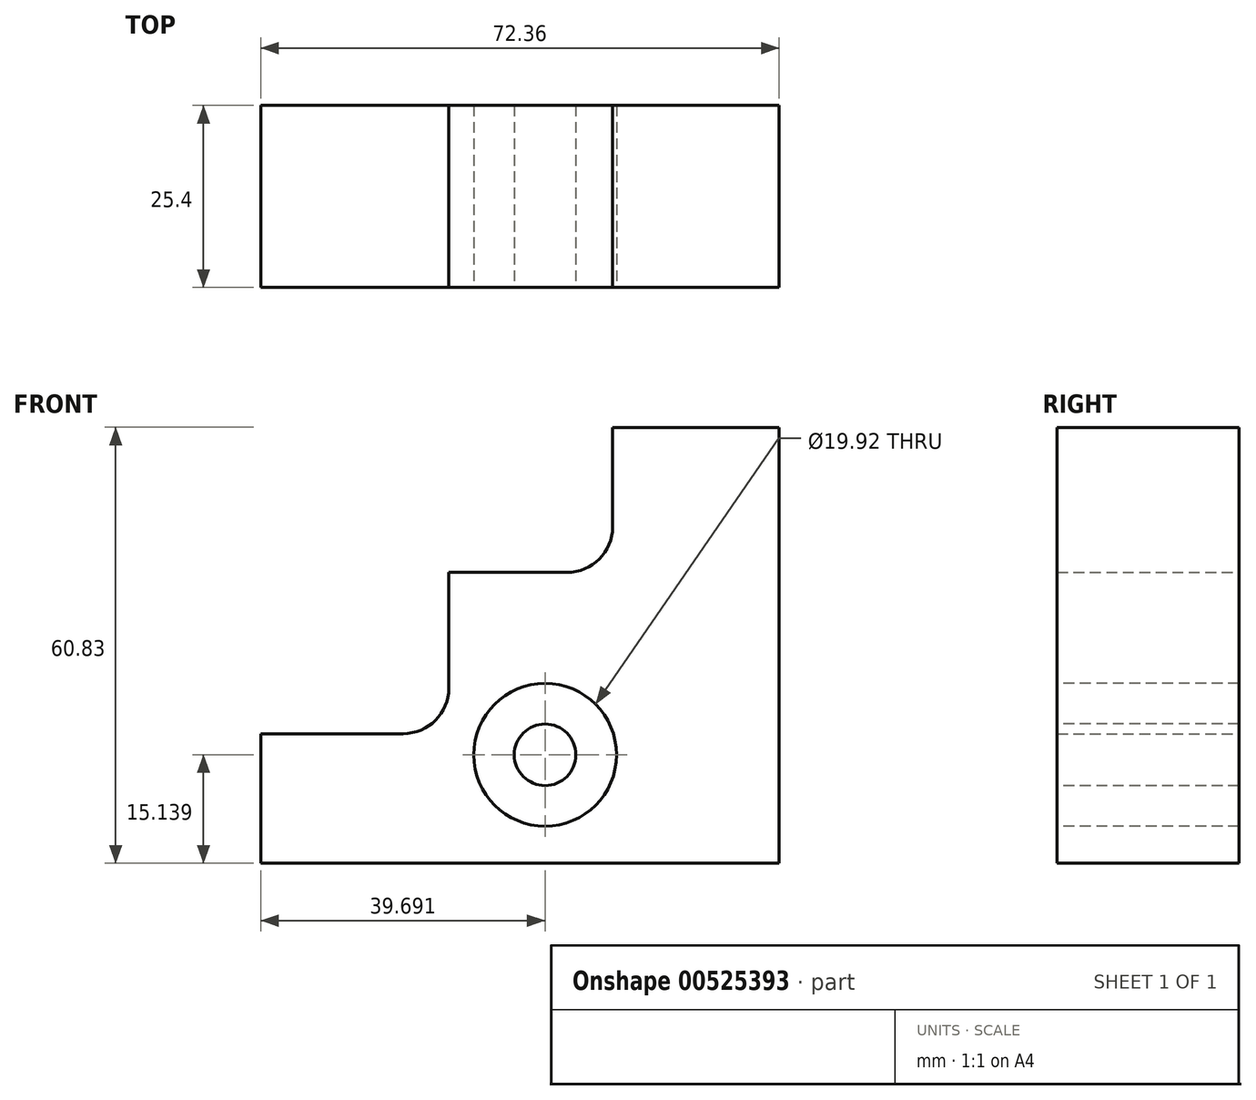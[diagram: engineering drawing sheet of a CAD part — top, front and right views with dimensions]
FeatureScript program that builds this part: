
annotation { "Feature Type Name" : "Feature", "Feature Type Description" : "" }
export const myFeature = defineFeature(function(context is Context, id is Id, definition is map)
    precondition{}
    {
        {
            var Q0;
            Q0=qCreatedBy(makeId("Front.planeOp"),FACE);
            var sketch = newSketch(context, id + "F0", { "sketchPlane" : qUnion([Q0])});
            skLineSegment(sketch, "E0", {"start": v(-54.48, 0) * mm, "end": v(-54.48, 18.09) * mm});
            skLineSegment(sketch, "E1", {"start": v(-54.48, 18.09) * mm, "end": v(-34.58, 18.09) * mm});
            skLineSegment(sketch, "E2", {"start": v(-28.23, 24.44) * mm, "end": v(-28.23, 40.58) * mm});
            skLineSegment(sketch, "E3", {"start": v(-27.48, 40.58) * mm, "end": v(-11.71, 40.58) * mm});
            skLineSegment(sketch, "E4", {"start": v(-5.36, 46.93) * mm, "end": v(-5.36, 60.83) * mm});
            skLineSegment(sketch, "E5", {"start": v(-5.36, 60.83) * mm, "end": v(17.88, 60.83) * mm});
            skLineSegment(sketch, "E6", {"start": v(17.88, 60.83) * mm, "end": v(17.88, 58.95) * mm});
            skLineSegment(sketch, "E7", {"start": v(17.88, 58.95) * mm, "end": v(17.88, 0) * mm});
            skLineSegment(sketch, "E8", {"start": v(17.88, 0) * mm, "end": v(-54.48, 0) * mm});
            skPoint(sketch, "E9.visualSharp", {"position": v(-28.23, 18.09) * mm});
            skArc(sketch, "E9.filletArc", {"start": v(-34.58, 18.09) * mm, "mid": v(-30.1, 19.95) * mm, "end": v(-28.23, 24.44) * mm});
            skPoint(sketch, "E10.visualSharp", {"position": v(-5.36, 40.58) * mm});
            skArc(sketch, "E10.filletArc", {"start": v(-11.71, 40.58) * mm, "mid": v(-7.22, 42.44) * mm, "end": v(-5.36, 46.93) * mm});
            skLineSegment(sketch, "E11", {"start": v(-28.23, 40.58) * mm, "end": v(-27.48, 40.58) * mm});
            skSolve(sketch);
        }
        {
            var Q0;
            Q0 = qSketchRegion(id + "F0", true);
            extrude(context, id + "F1", {"entities" : qUnion([Q0]), "depth" : 25.4 * mm, "offsetDistance" : 25.4 * mm});
        }
        {
            var Q0;
            Q0=makeQuery(id+"F1.opExtrude","CAP_FACE",FACE,{"disambiguationData":[OSD([sQuery(id+"F0.wireOp",EDGE,"E0"),sQuery(id+"F0.wireOp",EDGE,"E1"),sQuery(id+"F0.wireOp",EDGE,"E2"),sQuery(id+"F0.wireOp",EDGE,"E3"),sQuery(id+"F0.wireOp",EDGE,"E4"),sQuery(id+"F0.wireOp",EDGE,"E5"),sQuery(id+"F0.wireOp",EDGE,"E6"),sQuery(id+"F0.wireOp",EDGE,"E7"),sQuery(id+"F0.wireOp",EDGE,"E8"),sQuery(id+"F0.wireOp",EDGE,"E9.filletArc"),sQuery(id+"F0.wireOp",EDGE,"E10.filletArc"),sQuery(id+"F0.wireOp",EDGE,"E11")])],"isStart":false});
            var sketch = newSketch(context, id + "F2", { "sketchPlane" : qUnion([Q0])});
            skPoint(sketch, "E12.first.point", {"position": v(-14.79, 15.14) * mm});
            skPoint(sketch, "E12.second.point", {"position": v(0, 29.9) * mm});
            skPoint(sketch, "E12.third.point", {"position": v(3.4, 23.66) * mm});
            skCircle(sketch, "E13", {"center": v(-14.79, 15.14) * mm, "radius": 9.96 * mm});
            skCircle(sketch, "E14", {"center": v(-14.79, 15.14) * mm, "radius": 4.3 * mm});
            skSolve(sketch);
        }
        {
            var Q0;
            Q0=makeQuery(id+"F2.imprint","IMPRINT",FACE,{"disambiguationData":[TD([[makeQuery(id+"F2.imprint","IMPRINT",EDGE,{"derivedFrom":sQuery(id+"F2.wireOp",EDGE,"E13")}),1.0]])]});
            extrude(context, id + "F3", {"entities" : qUnion([Q0]), "operationType" : NewBodyOperationType.REMOVE, "oppositeDirection" : true, "depth" : 45.6 * mm, "offsetDistance" : 25 * mm});
        }
    });
